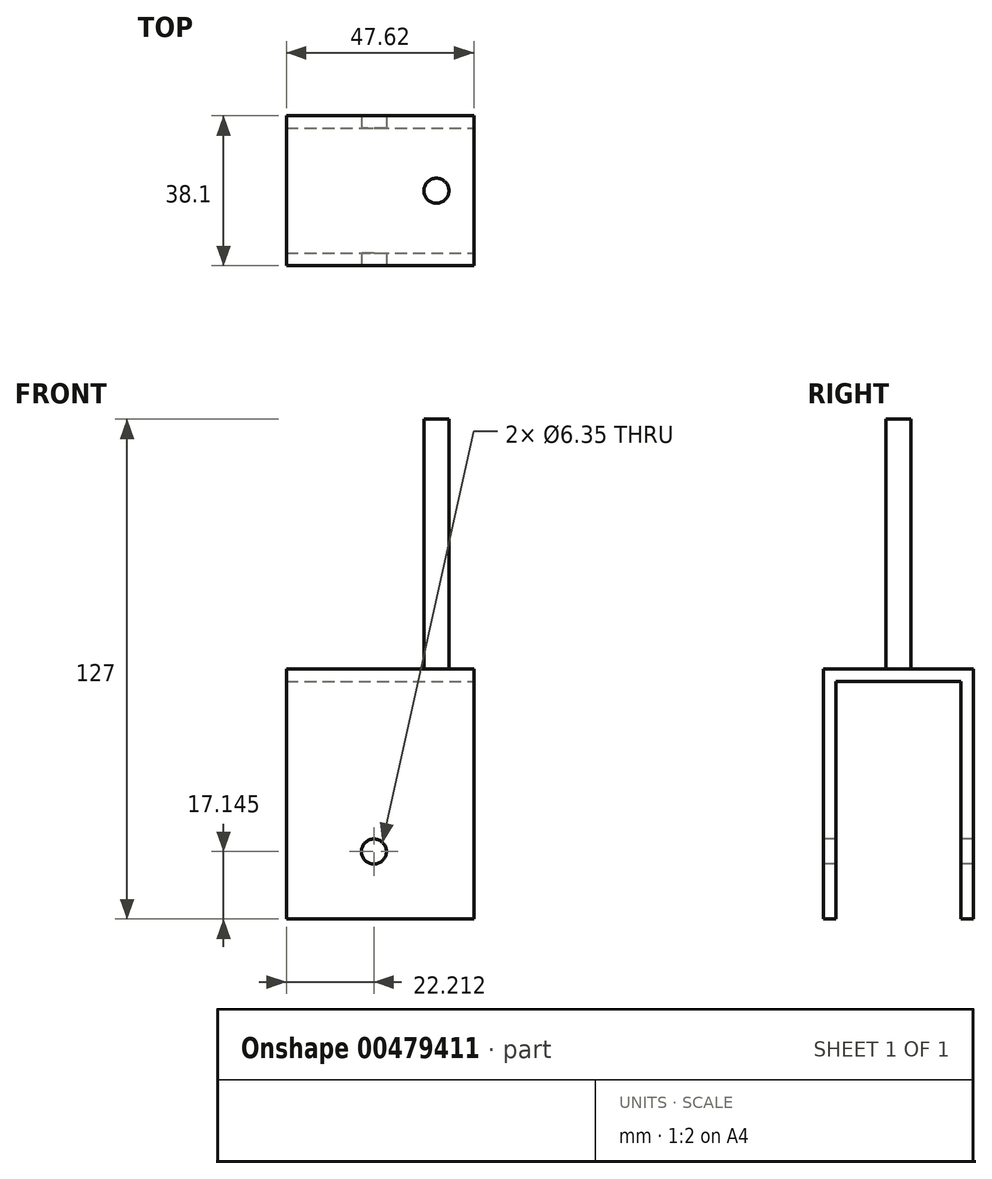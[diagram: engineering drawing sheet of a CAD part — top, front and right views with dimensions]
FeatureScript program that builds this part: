
annotation { "Feature Type Name" : "Feature", "Feature Type Description" : "" }
export const myFeature = defineFeature(function(context is Context, id is Id, definition is map)
    precondition{}
    {
        {
            var Q0;
            Q0=qCreatedBy(makeId("Top.planeOp"),FACE);
            var sketch = newSketch(context, id + "F0", { "sketchPlane" : qUnion([Q0])});
            skLineSegment(sketch, "E0.bottom", {"start": v(0, 0) * mm, "end": v(47.63, 0) * mm});
            skLineSegment(sketch, "E0.top", {"start": v(0, 38.1) * mm, "end": v(47.62, 38.1) * mm});
            skLineSegment(sketch, "E0.left", {"start": v(0, 0) * mm, "end": v(0, 38.1) * mm});
            skLineSegment(sketch, "E0.right", {"start": v(47.63, 0) * mm, "end": v(47.63, 38.1) * mm});
            skSolve(sketch);
        }
        {
            var Q0;
            Q0 = qSketchRegion(id + "F0", true);
            extrude(context, id + "F1", {"entities" : qUnion([Q0]), "depth" : 63.5 * mm, "offsetDistance" : 25.4 * mm});
        }
        {
            var Q0;
            Q0=makeQuery(id+"F1.opExtrude","SWEPT_FACE",FACE,{"disambiguationData":[OSD([sQuery(id+"F0.wireOp",EDGE,"E0.right")])]});
            var sketch = newSketch(context, id + "F2", { "sketchPlane" : qUnion([Q0])});
            skLineSegment(sketch, "E1.bottom", {"start": v(3.18, 0) * mm, "end": v(34.92, 0) * mm});
            skLineSegment(sketch, "E1.top", {"start": v(3.17, 60.33) * mm, "end": v(34.92, 60.33) * mm});
            skLineSegment(sketch, "E1.left", {"start": v(3.18, 0) * mm, "end": v(3.17, 60.33) * mm});
            skLineSegment(sketch, "E1.right", {"start": v(34.92, 0) * mm, "end": v(34.92, 60.33) * mm});
            skSolve(sketch);
        }
        {
            var Q0;
            Q0 = qSketchRegion(id + "F2", true);
            extrude(context, id + "F3", {"entities" : qUnion([Q0]), "operationType" : NewBodyOperationType.REMOVE, "oppositeDirection" : true, "depth" : 47.62 * mm, "offsetDistance" : 25.4 * mm});
        }
        {
            var Q0;
            Q0=makeQuery(id+"F1.opExtrude","CAP_FACE",FACE,{"disambiguationData":[OSD([sQuery(id+"F0.wireOp",EDGE,"E0.bottom"),sQuery(id+"F0.wireOp",EDGE,"E0.top"),sQuery(id+"F0.wireOp",EDGE,"E0.left"),sQuery(id+"F0.wireOp",EDGE,"E0.right")])],"isStart":false});
            var sketch = newSketch(context, id + "F4", { "sketchPlane" : qUnion([Q0])});
            skCircle(sketch, "E2", {"center": v(38.1, 19.05) * mm, "radius": 3.18 * mm});
            skSolve(sketch);
        }
        {
            var Q0;
            Q0 = qSketchRegion(id + "F4", true);
            extrude(context, id + "F5", {"entities" : qUnion([Q0]), "operationType" : NewBodyOperationType.ADD, "depth" : 63.5 * mm, "offsetDistance" : 25.4 * mm});
        }
        {
            var Q0;
            Q0=makeQuery(id+"F1.opExtrude","SWEPT_FACE",FACE,{"disambiguationData":[OSD([sQuery(id+"F0.wireOp",EDGE,"E0.bottom")])]});
            var sketch = newSketch(context, id + "F6", { "sketchPlane" : qUnion([Q0])});
            skCircle(sketch, "E3", {"center": v(22.21, 17.14) * mm, "radius": 3.18 * mm});
            skSolve(sketch);
        }
        {
            var Q0;
            Q0 = qSketchRegion(id + "F6", true);
            extrude(context, id + "F7", {"entities" : qUnion([Q0]), "operationType" : NewBodyOperationType.REMOVE, "oppositeDirection" : true, "depth" : 45.97 * mm, "offsetDistance" : 25.4 * mm});
        }
    });
